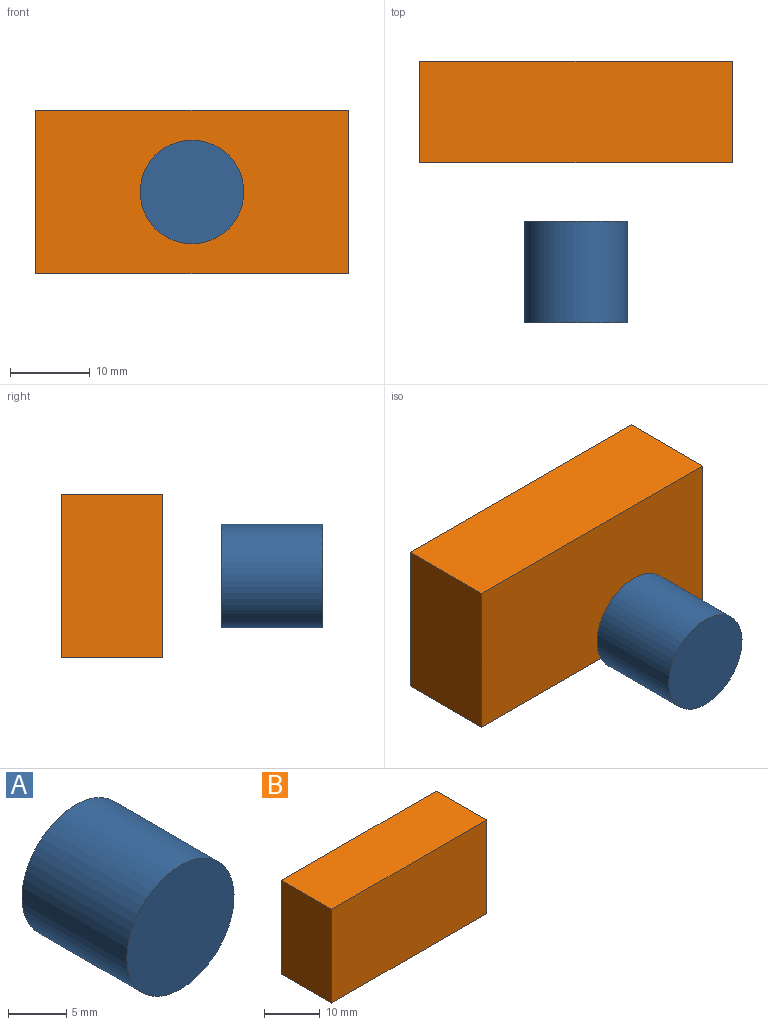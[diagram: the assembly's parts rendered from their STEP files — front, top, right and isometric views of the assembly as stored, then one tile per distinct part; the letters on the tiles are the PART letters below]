
ASSEMBLY  parts=2 mates=1
PART A: 3 faces, bbox 13x12.7x13 mm
  f0: cylinder r=6.49mm len=12.98mm, axis (0,1,0), area 517.8mm2, adj f1,f2
  f1: plane 12.98x12.98mm, normal (0,-1,0), area 132.3mm2, adj f0
  f2: plane 12.98x12.98mm, normal (0,1,0), area 132.3mm2, adj f0
PART B: 6 faces, bbox 39.2x12.7x20.5 mm
  f0: plane 20.51x12.7mm, normal (-1,0,0), area 260.4mm2, adj f1,f3,f4,f5
  f1: plane 39.15x12.7mm, normal (0,0,-1), area 497.2mm2, adj f0,f2,f4,f5
  f2: plane 20.51x12.7mm, normal (1,0,0), area 260.4mm2, adj f1,f3,f4,f5
  f3: plane 39.15x12.7mm, normal (0,0,1), area 497.2mm2, adj f0,f2,f4,f5
  f4: plane 39.15x20.51mm, normal (0,-1,0), area 802.9mm2, adj f0,f1,f2,f3
  f5: plane 39.15x20.51mm, normal (0,1,0), area 802.9mm2, adj f0,f1,f2,f3
PLACE A t=(-17.16,-28.49,-33.78)mm
PLACE B t=(16.95,-8.45,-33.9)mm fixed
MATE slider B.f4 <-> A.f0  axis (0,-1,0) through (-33.08,-21.15,28.55)mm
